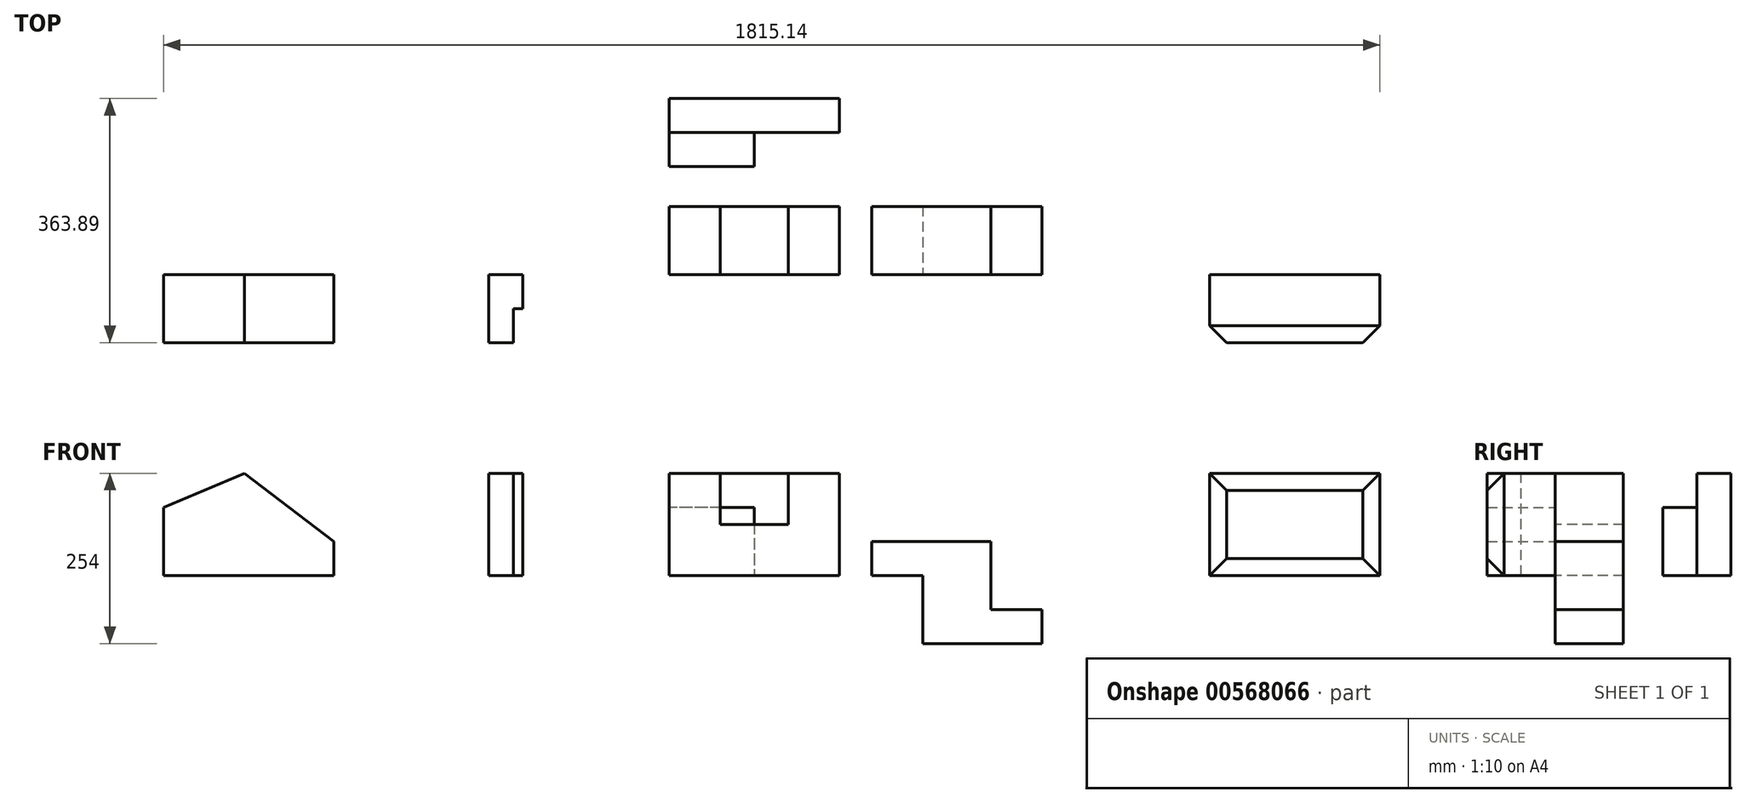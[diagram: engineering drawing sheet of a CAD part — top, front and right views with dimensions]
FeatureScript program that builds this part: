
annotation { "Feature Type Name" : "Feature", "Feature Type Description" : "" }
export const myFeature = defineFeature(function(context is Context, id is Id, definition is map)
    precondition{}
    {
        {
            var Q0;
            Q0=qCreatedBy(makeId("Front.planeOp"),FACE);
            var sketch = newSketch(context, id + "F0", { "sketchPlane" : qUnion([Q0])});
            skLineSegment(sketch, "E0", {"start": v(0, 0) * mm, "end": v(0, 152.4) * mm});
            skLineSegment(sketch, "E1", {"start": v(0, 152.4) * mm, "end": v(76.2, 152.4) * mm});
            skLineSegment(sketch, "E2", {"start": v(76.2, 152.4) * mm, "end": v(76.2, 76.2) * mm});
            skLineSegment(sketch, "E3", {"start": v(76.2, 76.2) * mm, "end": v(177.8, 76.2) * mm});
            skLineSegment(sketch, "E4", {"start": v(177.8, 76.2) * mm, "end": v(177.8, 152.4) * mm});
            skLineSegment(sketch, "E5", {"start": v(177.8, 152.4) * mm, "end": v(254, 152.4) * mm});
            skLineSegment(sketch, "E6", {"start": v(254, 152.4) * mm, "end": v(254, 0) * mm});
            skLineSegment(sketch, "E7", {"start": v(0, 0) * mm, "end": v(254, 0) * mm});
            skSolve(sketch);
        }
        {
            var Q0;
            Q0=makeQuery(id+"F0.imprint","IMPRINT",FACE,{"disambiguationData":[TD([[makeQuery(id+"F0.imprint","IMPRINT",EDGE,{"derivedFrom":sQuery(id+"F0.wireOp",EDGE,"E0")}),-1.0]])]});
            extrude(context, id + "F1", {"entities" : qUnion([Q0]), "oppositeDirection" : true, "depth" : 101.6 * mm, "offsetDistance" : 25.4 * mm});
        }
        {
            var Q0;
            Q0=qCreatedBy(makeId("Right.planeOp"),FACE);
            var sketch = newSketch(context, id + "F2", { "sketchPlane" : qUnion([Q0])});
            skLineSegment(sketch, "E8", {"start": v(160.69, 0) * mm, "end": v(262.29, 0) * mm});
            skLineSegment(sketch, "E9", {"start": v(262.29, 0) * mm, "end": v(262.29, 152.4) * mm});
            skLineSegment(sketch, "E10", {"start": v(262.29, 152.4) * mm, "end": v(211.49, 152.4) * mm});
            skLineSegment(sketch, "E11", {"start": v(211.49, 152.4) * mm, "end": v(211.49, 101.6) * mm});
            skLineSegment(sketch, "E12", {"start": v(211.49, 101.6) * mm, "end": v(160.69, 101.6) * mm});
            skLineSegment(sketch, "E13", {"start": v(160.69, 101.6) * mm, "end": v(160.69, 0) * mm});
            skSolve(sketch);
        }
        {
            var Q0;
            Q0 = qSketchRegion(id + "F2", true);
            extrude(context, id + "F3", {"entities" : qUnion([Q0]), "depth" : 254 * mm, "offsetDistance" : 25.4 * mm});
        }
        {
            var Q0;
            Q0=makeQuery(id+"F3.opExtrude","CAP_FACE",FACE,{"disambiguationData":[OSD([sQuery(id+"F2.wireOp",EDGE,"E8"),sQuery(id+"F2.wireOp",EDGE,"E9"),sQuery(id+"F2.wireOp",EDGE,"E10"),sQuery(id+"F2.wireOp",EDGE,"E11"),sQuery(id+"F2.wireOp",EDGE,"E12"),sQuery(id+"F2.wireOp",EDGE,"E13")])],"isStart":false});
            var sketch = newSketch(context, id + "F4", { "sketchPlane" : qUnion([Q0])});
            skLineSegment(sketch, "E14", {"start": v(211.49, 101.6) * mm, "end": v(211.49, 0) * mm});
            skSolve(sketch);
        }
        {
            var Q0;
            {var subQ0=sQuery(id+"F4.wireOp",EDGE,"E14");Q0=makeQuery(id+"F4.imprint","IMPRINT",FACE,{"disambiguationData":[TD([[makeQuery(id+"F4.imprint","IMPRINT",EDGE,{"derivedFrom":subQ0}),-1.0]])]});}
            extrude(context, id + "F5", {"entities" : qUnion([Q0]), "operationType" : NewBodyOperationType.REMOVE, "oppositeDirection" : true, "depth" : 127 * mm, "offsetDistance" : 25.4 * mm});
        }
        {
            var Q0;
            Q0=qCreatedBy(makeId("Front.planeOp"),FACE);
            var sketch = newSketch(context, id + "F6", { "sketchPlane" : qUnion([Q0])});
            skLineSegment(sketch, "E15", {"start": v(-269.41, 0) * mm, "end": v(-269.41, 152.4) * mm});
            skLineSegment(sketch, "E16", {"start": v(-269.41, 152.4) * mm, "end": v(-91.61, 152.4) * mm});
            skLineSegment(sketch, "E17", {"start": v(-91.61, 152.4) * mm, "end": v(-91.61, 50.8) * mm});
            skLineSegment(sketch, "E18", {"start": v(-91.61, 50.8) * mm, "end": v(-15.41, 50.8) * mm});
            skLineSegment(sketch, "E19", {"start": v(-15.41, 50.8) * mm, "end": v(-15.41, 0) * mm});
            skLineSegment(sketch, "E20", {"start": v(-15.41, 0) * mm, "end": v(-269.41, 0) * mm});
            skLineSegment(sketch, "E21", {"start": v(-269.41, 0) * mm, "end": v(-218.61, 0) * mm});
            skLineSegment(sketch, "E22", {"start": v(-218.61, 0) * mm, "end": v(-218.61, 152.4) * mm});
            skLineSegment(sketch, "E23", {"start": v(-218.61, 152.4) * mm, "end": v(-269.41, 152.4) * mm});
            skSolve(sketch);
        }
        {
            var Q0;
            Q0=makeQuery(id+"F6.imprint","IMPRINT",FACE,{"disambiguationData":[TD([[makeQuery(id+"F6.imprint","IMPRINT",EDGE,{"derivedFrom":sQuery(id+"F6.wireOp",EDGE,"E16")}),-1.0]])]});
            var Q1;
            Q1=makeQuery(id+"F6.imprint","IMPRINT",FACE,{"disambiguationData":[TD([[makeQuery(id+"F6.imprint","IMPRINT",EDGE,{"derivedFrom":sQuery(id+"F6.wireOp",EDGE,"E15")}),-1.0]])]});
            extrude(context, id + "F7", {"entities" : qUnion([Q0, Q1]), "depth" : 101.6 * mm, "offsetDistance" : 25.4 * mm});
        }
        {
            var Q0;
            Q0=makeQuery(id+"F7.opExtrude","SWEPT_FACE",FACE,{"disambiguationData":[OSD([sQuery(id+"F6.wireOp",EDGE,"E16"),sQuery(id+"F6.wireOp",EDGE,"E23")])]});
            var sketch = newSketch(context, id + "F8", { "sketchPlane" : qUnion([Q0])});
            skLineSegment(sketch, "E24", {"start": v(-232.59, -101.6) * mm, "end": v(-232.59, -50.8) * mm});
            skLineSegment(sketch, "E25", {"start": v(-232.59, -50.8) * mm, "end": v(-156.39, -50.8) * mm});
            skLineSegment(sketch, "E26", {"start": v(-156.39, -50.8) * mm, "end": v(-156.39, -101.6) * mm});
            skSolve(sketch);
        }
        {
            var Q0;
            Q0 = qSketchRegion(id + "F8", true);
            var Q1;
            {var subQ0=sQuery(id+"F8.wireOp",EDGE,"E24");Q1=makeQuery(id+"F8.imprint","IMPRINT",FACE,{"disambiguationData":[TD([[makeQuery(id+"F8.imprint","IMPRINT",EDGE,{"derivedFrom":subQ0}),-1.0]])]});}
            extrude(context, id + "F9", {"entities" : qUnion([Q0, Q1]), "operationType" : NewBodyOperationType.REMOVE, "oppositeDirection" : true, "depth" : 152.4 * mm, "offsetDistance" : 25.4 * mm});
        }
        {
            var Q0;
            Q0=qCreatedBy(makeId("Front.planeOp"),FACE);
            var sketch = newSketch(context, id + "F10", { "sketchPlane" : qUnion([Q0])});
            skLineSegment(sketch, "E27", {"start": v(302.5, 0) * mm, "end": v(302.5, 50.8) * mm});
            skLineSegment(sketch, "E28", {"start": v(302.5, 50.8) * mm, "end": v(480.3, 50.8) * mm});
            skLineSegment(sketch, "E29", {"start": v(480.3, 50.8) * mm, "end": v(480.3, -50.8) * mm});
            skLineSegment(sketch, "E30", {"start": v(480.3, -50.8) * mm, "end": v(556.5, -50.8) * mm});
            skLineSegment(sketch, "E31", {"start": v(556.5, -50.8) * mm, "end": v(556.5, -101.6) * mm});
            skLineSegment(sketch, "E32", {"start": v(556.5, -101.6) * mm, "end": v(378.7, -101.6) * mm});
            skLineSegment(sketch, "E33", {"start": v(378.7, -101.6) * mm, "end": v(378.7, 0) * mm});
            skLineSegment(sketch, "E34", {"start": v(378.7, 0) * mm, "end": v(302.5, 0) * mm});
            skSolve(sketch);
        }
        {
            var Q0;
            Q0 = qSketchRegion(id + "F10", true);
            extrude(context, id + "F11", {"entities" : qUnion([Q0]), "oppositeDirection" : true, "depth" : 101.6 * mm, "offsetDistance" : 25.4 * mm});
        }
        {
            var Q0;
            Q0=qCreatedBy(makeId("Front.planeOp"),FACE);
            var sketch = newSketch(context, id + "F12", { "sketchPlane" : qUnion([Q0])});
            skLineSegment(sketch, "E35", {"start": v(-754.58, 0) * mm, "end": v(-754.58, 101.6) * mm});
            skLineSegment(sketch, "E36", {"start": v(-754.58, 101.6) * mm, "end": v(-633.44, 152.4) * mm});
            skLineSegment(sketch, "E37", {"start": v(-633.44, 152.4) * mm, "end": v(-500.58, 50.8) * mm});
            skLineSegment(sketch, "E38", {"start": v(-500.58, 50.8) * mm, "end": v(-500.58, 0) * mm});
            skLineSegment(sketch, "E39", {"start": v(-500.58, 0) * mm, "end": v(-754.58, 0) * mm});
            skSolve(sketch);
        }
        {
            var Q0;
            Q0 = qSketchRegion(id + "F12", true);
            extrude(context, id + "F13", {"entities" : qUnion([Q0]), "depth" : 101.6 * mm, "offsetDistance" : 25.4 * mm});
        }
        {
            var Q0;
            Q0=qCreatedBy(makeId("Front.planeOp"),FACE);
            var sketch = newSketch(context, id + "F14", { "sketchPlane" : qUnion([Q0])});
            skLineSegment(sketch, "E40", {"start": v(806.56, 0) * mm, "end": v(806.56, 152.4) * mm});
            skLineSegment(sketch, "E41", {"start": v(806.56, 152.4) * mm, "end": v(1060.56, 152.4) * mm});
            skLineSegment(sketch, "E42", {"start": v(1060.56, 152.4) * mm, "end": v(1060.56, 0) * mm});
            skLineSegment(sketch, "E43", {"start": v(1060.56, 0) * mm, "end": v(806.56, 0) * mm});
            skSolve(sketch);
        }
        {
            var Q0;
            Q0 = qSketchRegion(id + "F14", true);
            extrude(context, id + "F15", {"entities" : qUnion([Q0]), "depth" : 101.6 * mm, "offsetDistance" : 25.4 * mm});
        }
        {
            var Q0;
            Q0=makeQuery(id+"F15.opExtrude","CAP_FACE",FACE,{"disambiguationData":[OSD([sQuery(id+"F14.wireOp",EDGE,"E40"),sQuery(id+"F14.wireOp",EDGE,"E41"),sQuery(id+"F14.wireOp",EDGE,"E42"),sQuery(id+"F14.wireOp",EDGE,"E43")])],"isStart":false});
            chamfer(context, id + "F16", {"entities" : qUnion([Q0]), "width" : 25.4 * mm, "tangentPropagation" : true});
        }
    });
